# Revit family: Grohe_PlumbingFixture_Eurosmart_SinkMixer_33202003a
name_source: partatom
category: Generic Models
revit_build: Autodesk Revit 2018 (Build: 20190510_1515(x64)
units: mm (PartAtom-declared; Revit-internal decimal feet)

## family parameters
Can host rebar = No
Cut with Voids When Loaded = No
Host = Face
OmniClass Number = 23.65.05.11.11
OmniClass Title = Water Supply Systems
Part Type = Normal
Room Calculation Point = No
Round Connector Dimension = Use Diameter
Shared = No

## types (1)
- 33202003
    ADACompliant = No
    Assembly Code = D2020300
    AssetType = Fixed
    BIMObjectName = Grohe_PlumbingFixture_Eurosmart_SinkMixer_33202003
    ClassificationName = Uniclass 2015
    ClassificationValue = Pr_40_20_87_84
    ColdWaterConnectionDiameter = 10 mm  [stored 0.0328084 ft]
    Color = Chrome
    Default Elevation = 1219 mm
    Description = Eurosmart
Single-lever sink mixer 1/2"
high spout
single hole installation
GROHE StarLight chrome finish
GROHE SilkMove 35 mm ceramic cartridge
integrated temperature limiter
mousseur
adjustable flow rate limiter
swivel tubular spout
swivel area: 150°
GROHE Zero isolated inner water ways - lead and nickel free
flexible connection hoses 3/8“
GROHE QuickFix Plus installation system
min. recommended pressure 1.0 bar
    DocumentationCertificates = https://www.bimstore.co
    DocumentationInstallationGuide = https://www.bimstore.co
    DocumentationLiterature = https://www.bimstore.co
    DocumentationMaintenance = https://www.bimstore.co
    DocumentationTechnical = https://www.bimstore.co
    DurationUnit = Years
    Ecojoy = No
    ExpectedLife = 0
    Features = Eurosmart
Single-lever sink mixer 1/2"
high spout
single hole installation
GROHE StarLight chrome finish
GROHE SilkMove 35 mm ceramic cartridge
integrated temperature limiter
mousseur
adjustable flow rate limiter
swivel tubular spout
swivel area: 150°
GROHE Zero isolated inner water ways - lead and nickel free
flexible connection hoses 3/8“
GROHE QuickFix Plus installation system
min. recommended pressure 1.0 bar
    Finish = Chrome
    HotWaterConnectionDiameter = 10 mm  [stored 0.0328084 ft]
    IfcExportAs = IfcPipeFitting
    IfcExportType = IfcPipeFittingType
    Keynote = S12
    LowEmittingMaterial = No
    Manufacturer = Grohe
    ManufacturerName = Grohe
    MasterformatNumber = 01 52 19
    MasterformatTitle = Sanitary Facilities
    Material = Plated Steel
    Model = Eurosmart - Single-lever sink mixer 1/2"
    ModelNumber = 33202003
    ModelReference = Eurosmart - Single-lever sink mixer 1/2"
    NBSDescription = Water supply fittings for sinks
    NBSObjectName = Grohe - Water supply fittings for sinks
    NBSReference = 45-35-70/345
    NominalDepth = 0 mm  [stored 0 ft]
    NominalHeight = 0 mm  [stored 0 ft]
    NominalLength = 0 mm  [stored 0 ft]
    ProductDocumentationLink = https://www.bimstore.co
    ProductPageURL = https://www.grohe.co.uk
    ProductionYear = 2020
    Type Comments = 33202003
    TypeName = Eurosmart - Single-lever sink mixer 1/2"
    URL = https://www.grohe.co.uk
    WarrantyDurationLabor = 0
    WarrantyDurationParts = 0
    WarrantyDurationUnit = Years
    _BSBibleVersion = 16
    _BimSpecGuid = 0
    _CurrentRevision = 1
    _DistributedBy = www.bimstore.co

note: [stored X ft] marks values corroborated as IEEE doubles in the binary element streams (Revit-internal decimal feet)

## geometry (parser evidence)
native form markers: Sweep x1
no freeform markers — native parametric forms only
